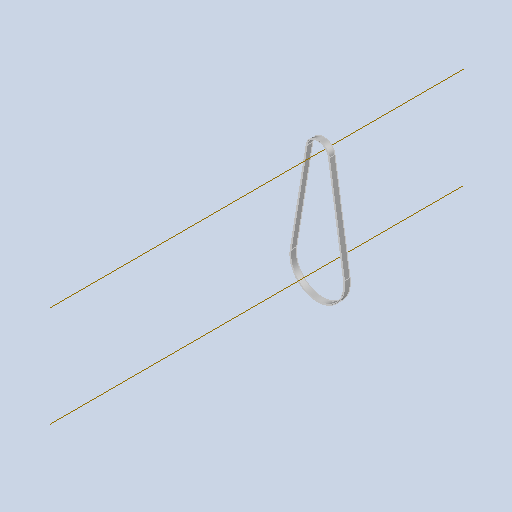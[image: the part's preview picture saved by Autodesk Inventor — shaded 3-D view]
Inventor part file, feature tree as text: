
AUTODESK INVENTOR PART (.ipt)
format: ipt  version: 2025.2 (Build 292293000, 293)  size: 97,280 bytes
history: native  units: mm (DEFAULTED — no unit token found)
features: other x4, plane x2, sketch x1, sweep x1
ambient origin geometry x8: Origin, YZ Plane, XZ Plane, XY Plane, X Axis, Y Axis, Z Axis, Center Point
bodies: Solid1 (feature_tree)
feature tree (8):
  sketch  "Sketch Path"  dims[d0=4.0mm d2=0.0mm d4=0.3mm d5=0.3mm d6=0.0mm d7=0.0mm d8=0.0mm d9=0.0mm d10=0.0mm d11=0.0mm]
  other  "Cross Section Plane"
  other  "Work Axis1"
  other  "Work Axis2"
  plane  "Work Plane2"
  plane  "Work Plane3"
  sweep  "Belt"
  other  "Cross Section"
